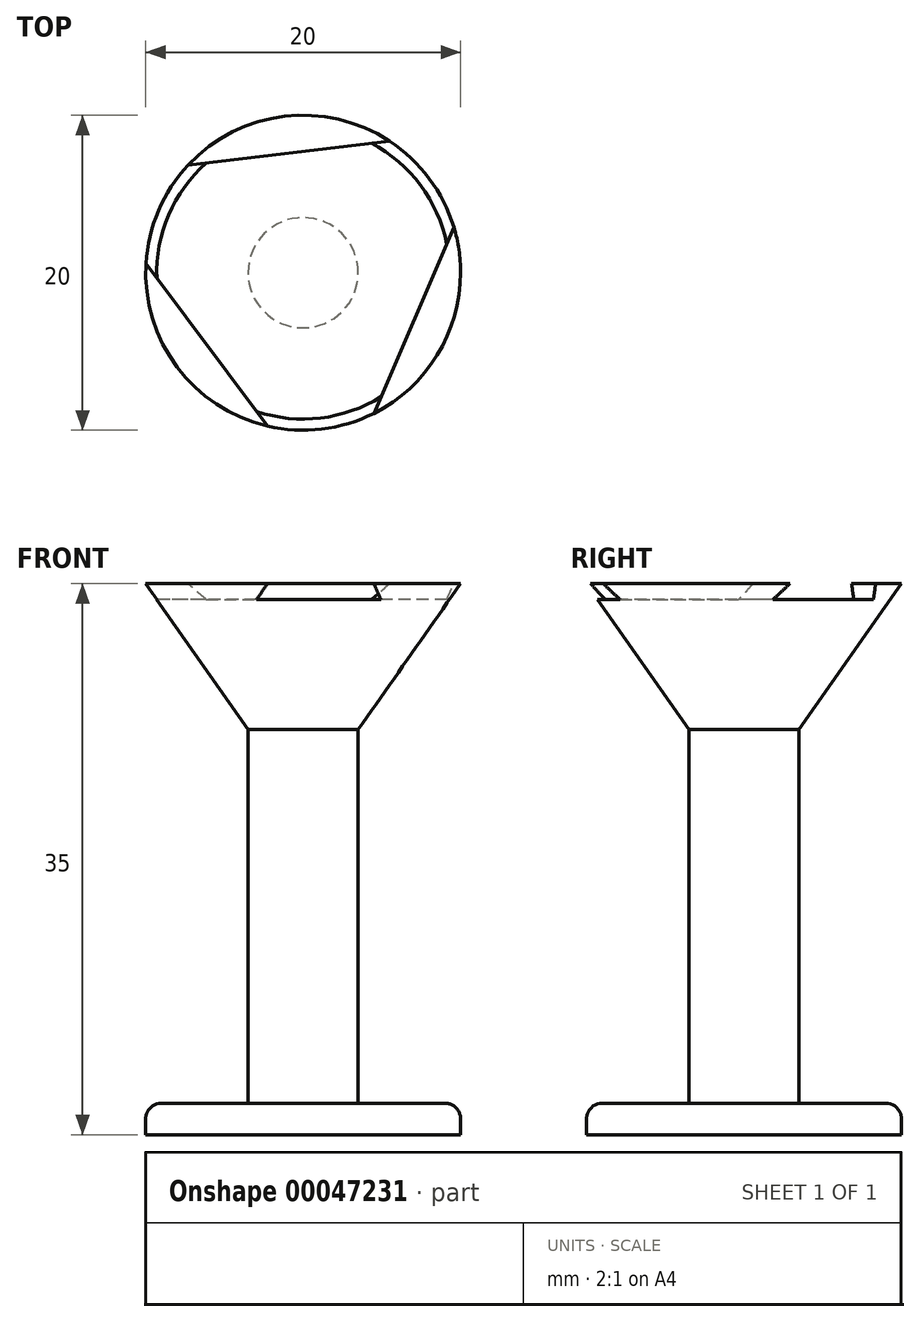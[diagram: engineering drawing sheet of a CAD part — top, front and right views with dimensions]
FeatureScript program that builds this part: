
annotation { "Feature Type Name" : "Feature", "Feature Type Description" : "" }
export const myFeature = defineFeature(function(context is Context, id is Id, definition is map)
    precondition{}
    {
        {
            var Q0;
            Q0=qCreatedBy(makeId("Top.planeOp"),FACE);
            var sketch = newSketch(context, id + "F0", { "sketchPlane" : qUnion([Q0])});
            skCircle(sketch, "E0", {"center": v(0, 0) * mm, "radius": 10 * mm});
            skSolve(sketch);
        }
        {
            var Q0;
            Q0=makeQuery(id+"F0.imprint","IMPRINT",FACE,{"disambiguationData":[TD([[makeQuery(id+"F0.imprint","IMPRINT",EDGE,{"derivedFrom":sQuery(id+"F0.wireOp",EDGE,"E0")}),1.0]])]});
            extrude(context, id + "F1", {"entities" : qUnion([Q0]), "depth" : 2 * mm});
        }
        {
            var Q0;
            Q0=qCreatedBy(makeId("Front.planeOp"),FACE);
            var sketch = newSketch(context, id + "F2", { "sketchPlane" : qUnion([Q0])});
            skLineSegment(sketch, "E1", {"start": v(0, 0) * mm, "end": v(0, 45) * mm, "construction": true});
            skLineSegment(sketch, "E2", {"start": v(-10, 45) * mm, "end": v(10, 45) * mm, "construction": true});
            skLineSegment(sketch, "E3", {"start": v(-3.5, 35) * mm, "end": v(3.5, 35) * mm, "construction": true});
            skLineSegment(sketch, "E4.0", {"start": v(-10, 2) * mm, "end": v(10, 2) * mm, "construction": true});
            skPoint(sketch, "E5.rect.middle", {"position": v(0, 45) * mm});
            skLineSegment(sketch, "E6", {"start": v(-10, 35) * mm, "end": v(-3.5, 25.73) * mm});
            skLineSegment(sketch, "E7", {"start": v(-10, 35) * mm, "end": v(0, 35) * mm});
            skLineSegment(sketch, "E8", {"start": v(0, 35) * mm, "end": v(0, 2) * mm});
            skLineSegment(sketch, "E9", {"start": v(-3.5, 25.73) * mm, "end": v(-3.5, 2) * mm});
            skLineSegment(sketch, "E10", {"start": v(-3.5, 2) * mm, "end": v(0, 2) * mm});
            skSolve(sketch);
        }
        {
            var Q0;
            Q0=makeQuery(id+"F1.opExtrude","CAP_EDGE",EDGE,{"disambiguationData":[OSD([sQuery(id+"F0.wireOp",EDGE,"E0")])],"isStart":false});
            var Q1;
            Q1=makeQuery(id+"FvqPasuWNJc833q_1.opExtrude","SWEPT_EDGE",EDGE,{"disambiguationData":[OSD([sQuery(id+"F2.wireOp",EDGE,"ea9f52d2-23db-4adb-a2b5-649324e33694"),sQuery(id+"F2.wireOp",EDGE,"E6")])]});
            var Q2;
            Q2=makeQuery(id+"FvqPasuWNJc833q_1.opExtrude","SWEPT_EDGE",EDGE,{"disambiguationData":[OSD([sQuery(id+"F2.wireOp",EDGE,"10ce7b36-c59c-4cd9-a3f4-747a7723e4ff0.MirrorCS"),sQuery(id+"F2.wireOp",EDGE,"bf594ac4-af1f-4a43-adda-506e7a3d41d30.MirrorCS")])]});
            var Q3;
            {var subQ0=sQuery(id+"F2.wireOp",EDGE,"E5.rect.bottom");var subQ1=sQuery(id+"F2.wireOp",EDGE,"E5.rect.left");var subQ2=sQuery(id+"F2.wireOp",EDGE,"bf594ac4-af1f-4a43-adda-506e7a3d41d30.MirrorCS");Q3=makeQuery(id+"F8HMD6Pr1riJxlU_1.boolean.opBoolean","MERGE",EDGE,{"derivedFrom":[makeQuery(id+"FvqPasuWNJc833q_1.opExtrude","SWEPT_EDGE",EDGE,{"disambiguationData":[OSD([subQ0,subQ1,subQ2])]}),makeQuery(id+"F8HMD6Pr1riJxlU_1.opExtrude","SWEPT_EDGE",EDGE,{"disambiguationData":[OSD([subQ0,subQ1,subQ2])]})]});}
            var Q4;
            {var subQ0=sQuery(id+"F2.wireOp",EDGE,"E5.rect.bottom");var subQ1=sQuery(id+"F2.wireOp",EDGE,"E5.rect.right");var subQ2=sQuery(id+"F2.wireOp",EDGE,"E6");Q4=makeQuery(id+"F8HMD6Pr1riJxlU_1.boolean.opBoolean","MERGE",EDGE,{"derivedFrom":[makeQuery(id+"FvqPasuWNJc833q_1.opExtrude","SWEPT_EDGE",EDGE,{"disambiguationData":[OSD([subQ0,subQ1,subQ2])]}),makeQuery(id+"F8HMD6Pr1riJxlU_1.opExtrude","SWEPT_EDGE",EDGE,{"disambiguationData":[OSD([subQ0,subQ1,subQ2])]})]});}
            var Q5;
            Q5=makeQuery(id+"FvqPasuWNJc833q_1.opExtrude","CAP_EDGE",EDGE,{"disambiguationData":[OSD([sQuery(id+"F2.wireOp",EDGE,"9131b7b5-3c03-4f48-9a4c-9dbebe6fd0da")])],"isStart":false});
            var Q6;
            Q6=makeQuery(id+"FvqPasuWNJc833q_1.opExtrude","SWEPT_EDGE",EDGE,{"disambiguationData":[OSD([sQuery(id+"F2.wireOp",EDGE,"10ce7b36-c59c-4cd9-a3f4-747a7723e4ff0.MirrorCS"),sQuery(id+"F2.wireOp",EDGE,"9131b7b5-3c03-4f48-9a4c-9dbebe6fd0da")])]});
            var Q7;
            Q7=makeQuery(id+"FvqPasuWNJc833q_1.opExtrude","SWEPT_EDGE",EDGE,{"disambiguationData":[OSD([sQuery(id+"F2.wireOp",EDGE,"ea9f52d2-23db-4adb-a2b5-649324e33694"),sQuery(id+"F2.wireOp",EDGE,"9131b7b5-3c03-4f48-9a4c-9dbebe6fd0da")])]});
            var Q8;
            Q8=makeQuery(id+"FvqPasuWNJc833q_1.opExtrude","CAP_EDGE",EDGE,{"disambiguationData":[OSD([sQuery(id+"F2.wireOp",EDGE,"9131b7b5-3c03-4f48-9a4c-9dbebe6fd0da")])],"isStart":true});
            fillet(context, id + "F3", {"entities" : qUnion([Q0, Q1, Q2, Q3, Q4, Q5, Q6, Q7, Q8]), "radius" : 1 * mm, "tangentPropagation" : true, "allowEdgeOverflow" : false});
        }
        {
            var Q0;
            Q0=makeQuery(id+"F2.imprint","IMPRINT",FACE,{"disambiguationData":[TD([[makeQuery(id+"F2.imprint","IMPRINT",EDGE,{"derivedFrom":sQuery(id+"F2.wireOp",EDGE,"E6")}),1.0]])]});
            var Q1;
            Q1=sQuery(id+"F2.wireOp",EDGE,"E8");
            revolve(context, id + "F4", {"operationType" : NewBodyOperationType.ADD, "entities" : qUnion([Q0]), "axis" : qUnion([Q1]), "revolveType" : RevolveType.FULL});
        }
        {
            var Q0;
            Q0=makeQuery(id+"F4.opRevolve","SWEPT_FACE",FACE,{"disambiguationData":[OSD([sQuery(id+"F2.wireOp",EDGE,"E7")])]});
            var sketch = newSketch(context, id + "F5", { "sketchPlane" : qUnion([Q0])});
            skLineSegment(sketch, "E11", {"start": v(12.25, 9.16) * mm, "end": v(1.8, -15.2) * mm});
            skLineSegment(sketch, "E12", {"start": v(1.8, -15.2) * mm, "end": v(-14.06, 6.03) * mm});
            skLineSegment(sketch, "E13", {"start": v(-14.06, 6.03) * mm, "end": v(12.25, 9.16) * mm});
            skLineSegment(sketch, "E14", {"start": v(-14.06, 6.03) * mm, "end": v(0, 0) * mm, "construction": true});
            skLineSegment(sketch, "E15", {"start": v(0, 0) * mm, "end": v(1.8, -15.2) * mm, "construction": true});
            skLineSegment(sketch, "E16", {"start": v(12.25, 9.16) * mm, "end": v(0, 0) * mm, "construction": true});
            skPoint(sketch, "E17", {"position": v(0, 0) * mm});
            skSolve(sketch);
        }
        {
            var Q0;
            Q0 = qSketchRegion(id + "F5", true);
            extrude(context, id + "F6", {"entities" : qUnion([Q0]), "operationType" : NewBodyOperationType.REMOVE, "oppositeDirection" : true, "depth" : 1 * mm});
        }
    });
